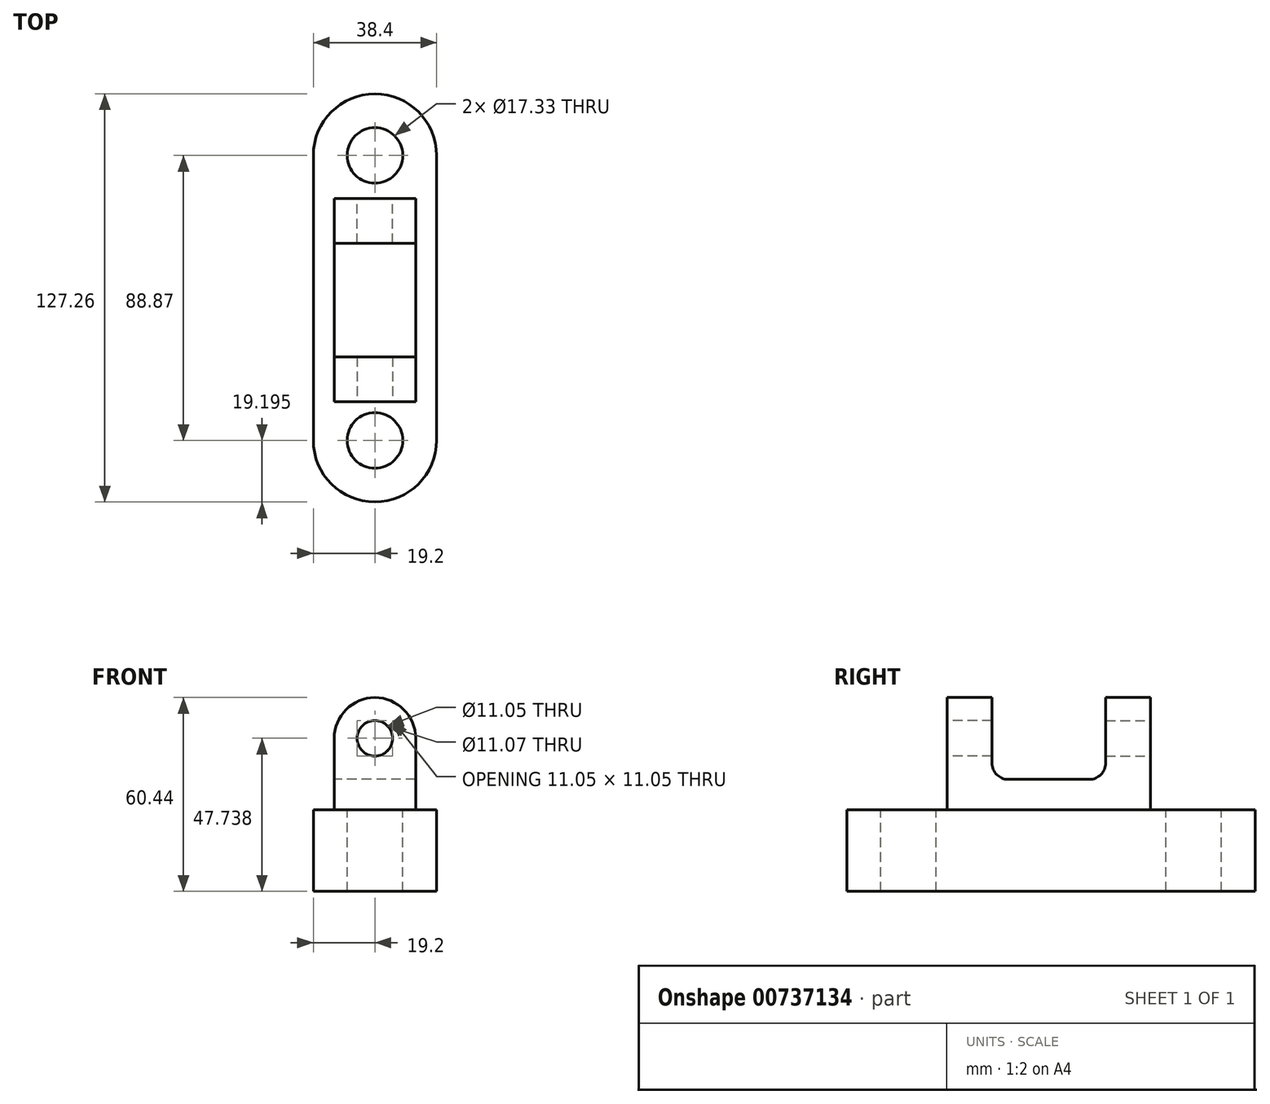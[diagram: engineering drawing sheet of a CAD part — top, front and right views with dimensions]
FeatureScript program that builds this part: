
annotation { "Feature Type Name" : "Feature", "Feature Type Description" : "" }
export const myFeature = defineFeature(function(context is Context, id is Id, definition is map)
    precondition{}
    {
        {
            var Q0;
            Q0=qCreatedBy(makeId("Top.planeOp"),FACE);
            var sketch = newSketch(context, id + "F0", { "sketchPlane" : qUnion([Q0])});
            skLineSegment(sketch, "E0.left", {"start": v(-19.2, 44.44) * mm, "end": v(-19.2, -44.44) * mm});
            skLineSegment(sketch, "E0.right", {"start": v(19.2, 44.44) * mm, "end": v(19.2, -44.44) * mm});
            skPoint(sketch, "E0.middle", {"position": v(0, 0) * mm});
            skArc(sketch, "E1", {"start": v(19.2, 44.44) * mm, "mid": v(0, 63.63) * mm, "end": v(-19.2, 44.44) * mm});
            skArc(sketch, "E2", {"start": v(-19.2, -44.44) * mm, "mid": v(0, -63.63) * mm, "end": v(19.2, -44.44) * mm});
            skCircle(sketch, "E3", {"center": v(0, 44.44) * mm, "radius": 8.66 * mm});
            skCircle(sketch, "E4", {"center": v(0, -44.44) * mm, "radius": 8.66 * mm});
            skSolve(sketch);
        }
        {
            var Q0;
            Q0=makeQuery(id+"F0.imprint","IMPRINT",FACE,{"disambiguationData":[TD([[makeQuery(id+"F0.imprint","IMPRINT",EDGE,{"derivedFrom":sQuery(id+"F0.wireOp",EDGE,"E0.left")}),1.0]])]});
            extrude(context, id + "F1", {"entities" : qUnion([Q0]), "oppositeDirection" : true, "depth" : 25.4 * mm, "offsetDistance" : 25.4 * mm});
        }
        {
            var Q0;
            Q0=qCreatedBy(makeId("Right.planeOp"),FACE);
            var sketch = newSketch(context, id + "F2", { "sketchPlane" : qUnion([Q0])});
            skLineSegment(sketch, "E5", {"start": v(-32.35, 0) * mm, "end": v(-32.35, 35.04) * mm});
            skLineSegment(sketch, "E6", {"start": v(-32.35, 35.04) * mm, "end": v(-18.4, 35.04) * mm});
            skLineSegment(sketch, "E7", {"start": v(-18.4, 35.04) * mm, "end": v(-18.4, 9.53) * mm});
            skLineSegment(sketch, "E8", {"start": v(-18.4, 9.53) * mm, "end": v(17.05, 9.53) * mm});
            skLineSegment(sketch, "E9", {"start": v(17.05, 9.53) * mm, "end": v(17.05, 35.04) * mm});
            skLineSegment(sketch, "E10", {"start": v(17.05, 35.04) * mm, "end": v(31.01, 35.04) * mm});
            skLineSegment(sketch, "E11", {"start": v(31.01, 35.04) * mm, "end": v(31.01, 0) * mm});
            skLineSegment(sketch, "E12", {"start": v(-32.35, 0) * mm, "end": v(31.01, 0) * mm});
            skSolve(sketch);
        }
        {
            var Q0;
            Q0=makeQuery(id+"F2.imprint","IMPRINT",FACE,{"disambiguationData":[TD([[makeQuery(id+"F2.imprint","IMPRINT",EDGE,{"derivedFrom":sQuery(id+"F2.wireOp",EDGE,"E5")}),-1.0]])]});
            extrude(context, id + "F3", {"entities" : qUnion([Q0]), "operationType" : NewBodyOperationType.ADD, "endBound" : BoundingType.SYMMETRIC, "depth" : 25.4 * mm, "offsetDistance" : 25.4 * mm});
        }
        {
            var Q0;
            Q0=makeQuery(id+"F3.opExtrude","SWEPT_EDGE",EDGE,{"disambiguationData":[OSD([sQuery(id+"F2.wireOp",EDGE,"E7"),sQuery(id+"F2.wireOp",EDGE,"E8")])]});
            fillet(context, id + "F4", {"entities" : qUnion([Q0]), "radius" : 5.08 * mm, "tangentPropagation" : true, "allowEdgeOverflow" : false});
        }
        {
            var Q0;
            Q0=makeQuery(id+"F3.opExtrude","SWEPT_EDGE",EDGE,{"disambiguationData":[OSD([sQuery(id+"F2.wireOp",EDGE,"E8"),sQuery(id+"F2.wireOp",EDGE,"E9")])]});
            fillet(context, id + "F5", {"entities" : qUnion([Q0]), "radius" : 5.08 * mm, "tangentPropagation" : true, "allowEdgeOverflow" : false});
        }
        {
            var Q0;
            Q0=makeQuery(id+"F3.opExtrude","CAP_EDGE",EDGE,{"disambiguationData":[OSD([sQuery(id+"F2.wireOp",EDGE,"E6")])],"isStart":false});
            fillet(context, id + "F6", {"entities" : qUnion([Q0]), "radius" : 12.7 * mm, "tangentPropagation" : true, "allowEdgeOverflow" : false});
        }
        {
            var Q0;
            Q0=makeQuery(id+"F3.opExtrude","CAP_EDGE",EDGE,{"disambiguationData":[OSD([sQuery(id+"F2.wireOp",EDGE,"E6")])],"isStart":true});
            fillet(context, id + "F7", {"entities" : qUnion([Q0]), "radius" : 12.7 * mm, "tangentPropagation" : true, "allowEdgeOverflow" : false});
        }
        {
            var Q0;
            Q0=makeQuery(id+"F3.opExtrude","CAP_EDGE",EDGE,{"disambiguationData":[OSD([sQuery(id+"F2.wireOp",EDGE,"E10")])],"isStart":false});
            fillet(context, id + "F8", {"entities" : qUnion([Q0]), "radius" : 12.7 * mm, "tangentPropagation" : true, "allowEdgeOverflow" : false});
        }
        {
            var Q0;
            Q0=makeQuery(id+"F3.opExtrude","CAP_EDGE",EDGE,{"disambiguationData":[OSD([sQuery(id+"F2.wireOp",EDGE,"E10")])],"isStart":true});
            fillet(context, id + "F9", {"entities" : qUnion([Q0]), "radius" : 12.7 * mm, "tangentPropagation" : true, "allowEdgeOverflow" : false});
        }
        {
            var Q0;
            Q0=makeQuery(id+"F3.opExtrude","SWEPT_FACE",FACE,{"disambiguationData":[OSD([sQuery(id+"F2.wireOp",EDGE,"E11")])]});
            var sketch = newSketch(context, id + "F10", { "sketchPlane" : qUnion([Q0])});
            skCircle(sketch, "E13", {"center": v(0, 22.34) * mm, "radius": 5.53 * mm});
            skSolve(sketch);
        }
        {
            var Q0;
            Q0=makeQuery(id+"F10.imprint","IMPRINT",FACE,{"disambiguationData":[TD([[makeQuery(id+"F10.imprint","IMPRINT",EDGE,{"derivedFrom":sQuery(id+"F10.wireOp",EDGE,"E13")}),1.0]])]});
            var Q1;
            Q1=sQuery(id+"F10.wireOp",EDGE,"E13");
            extrude(context, id + "F11", {"entities" : qUnion([Q0]), "operationType" : NewBodyOperationType.REMOVE, "surfaceEntities" : qUnion([Q1]), "oppositeDirection" : true, "depth" : 25.4 * mm, "offsetDistance" : 25.4 * mm});
        }
        {
            var Q0;
            Q0=makeQuery(id+"F3.opExtrude","SWEPT_FACE",FACE,{"disambiguationData":[OSD([sQuery(id+"F2.wireOp",EDGE,"E5")])]});
            var sketch = newSketch(context, id + "F12", { "sketchPlane" : qUnion([Q0])});
            skCircle(sketch, "E14", {"center": v(0, 22.34) * mm, "radius": 5.53 * mm});
            skSolve(sketch);
        }
        {
            var Q0;
            Q0 = qSketchRegion(id + "F12", true);
            extrude(context, id + "F13", {"entities" : qUnion([Q0]), "operationType" : NewBodyOperationType.REMOVE, "oppositeDirection" : true, "depth" : 25.4 * mm, "offsetDistance" : 25.4 * mm});
        }
    });
